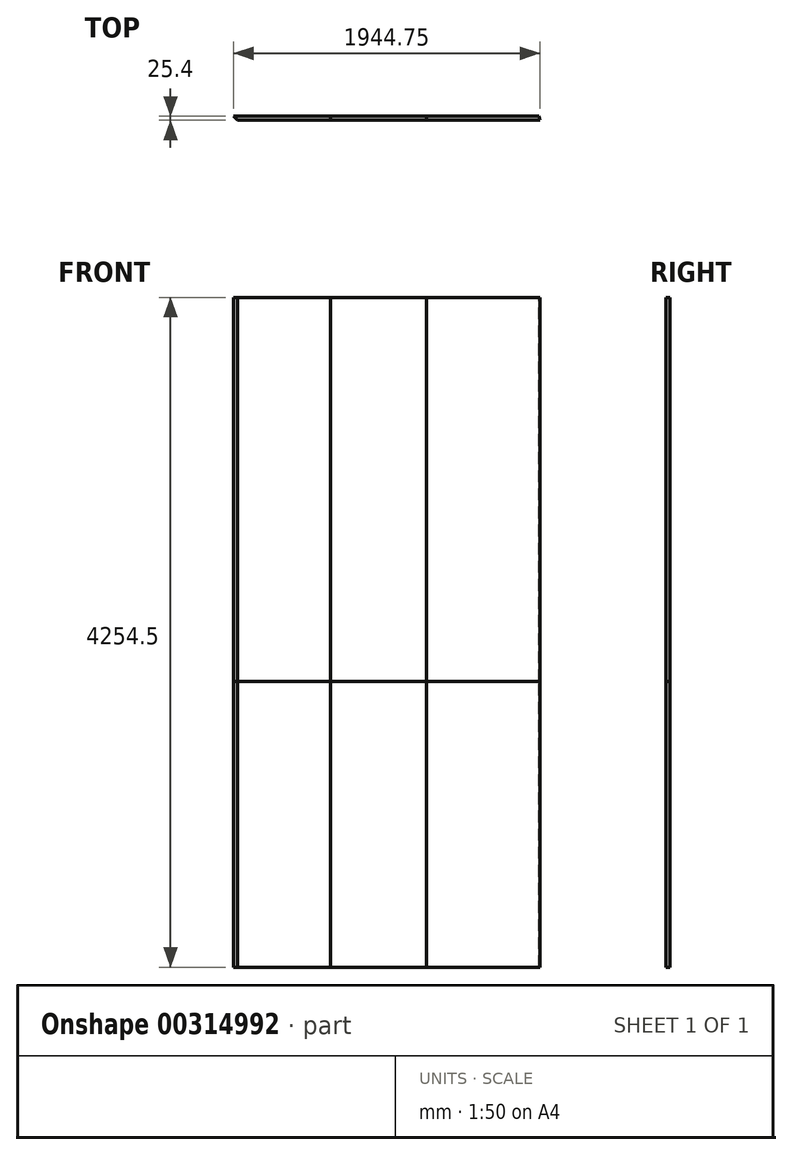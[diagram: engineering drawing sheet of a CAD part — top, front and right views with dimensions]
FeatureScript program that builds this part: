
annotation { "Feature Type Name" : "Feature", "Feature Type Description" : "" }
export const myFeature = defineFeature(function(context is Context, id is Id, definition is map)
    precondition{}
    {
        {
            var Q0;
            Q0=qCreatedBy(makeId("Top.planeOp"),FACE);
            var sketch = newSketch(context, id + "F0", { "sketchPlane" : qUnion([Q0])});
            skLineSegment(sketch, "E0", {"start": v(0, 0) * mm, "end": v(25.4, -25.4) * mm});
            skLineSegment(sketch, "E1", {"start": v(25.4, -25.4) * mm, "end": v(615.95, -25.4) * mm});
            skLineSegment(sketch, "E2", {"start": v(615.95, -25.4) * mm, "end": v(1225.55, -25.4) * mm});
            skLineSegment(sketch, "E3", {"start": v(1225.55, -25.4) * mm, "end": v(1944.75, -25.4) * mm});
            skLineSegment(sketch, "E4", {"start": v(1944.75, -25.4) * mm, "end": v(1944.75, 0) * mm, "construction": true});
            skLineSegment(sketch, "E5", {"start": v(1944.75, 0) * mm, "end": v(0, 0) * mm});
            skLineSegment(sketch, "E6", {"start": v(615.95, -25.4) * mm, "end": v(615.95, 0) * mm});
            skLineSegment(sketch, "E7", {"start": v(1502.86, -229.9) * mm, "end": v(1502.86, -380) * mm});
            skLineSegment(sketch, "E8", {"start": v(1225.55, 0) * mm, "end": v(1225.55, -25.4) * mm});
            skLineSegment(sketch, "E9", {"start": v(1944.75, -25.4) * mm, "end": v(1937.77, 0) * mm});
            skSolve(sketch);
        }
        {
            var Q0;
            {var subQ0=sQuery(id+"F0.wireOp",EDGE,"E0");Q0=makeQuery(id+"F0.imprint","IMPRINT",FACE,{"disambiguationData":[TD([[makeQuery(id+"F0.imprint","IMPRINT",EDGE,{"derivedFrom":subQ0}),1.0]])]});}
            extrude(context, id + "F1", {"entities" : qUnion([Q0]), "oppositeDirection" : true, "depth" : 2438.4 * mm});
        }
        {
            var Q0;
            Q0=makeQuery(id+"F0.imprint","IMPRINT",FACE,{"disambiguationData":[TD([[makeQuery(id+"F0.imprint","IMPRINT",EDGE,{"derivedFrom":sQuery(id+"F0.wireOp",EDGE,"E2")}),1.0]])]});
            var Q1;
            Q1=makeQuery(id+"F1.opExtrude","CAP_FACE",FACE,{"disambiguationData":[OSD([sQuery(id+"F0.wireOp",EDGE,"E0"),sQuery(id+"F0.wireOp",EDGE,"E1"),sQuery(id+"F0.wireOp",EDGE,"E5"),sQuery(id+"F0.wireOp",EDGE,"E6")])],"isStart":false});
            extrude(context, id + "F2", {"entities" : qUnion([Q0]), "endBound" : BoundingType.UP_TO_SURFACE, "oppositeDirection" : true, "endBoundEntityFace" : qUnion([Q1]), "depth" : 25.4 * mm});
        }
        {
            var Q0;
            Q0=makeQuery(id+"F0.imprint","IMPRINT",FACE,{"disambiguationData":[TD([[makeQuery(id+"F0.imprint","IMPRINT",EDGE,{"derivedFrom":sQuery(id+"F0.wireOp",EDGE,"E3")}),1.0]])]});
            var Q1;
            Q1=makeQuery(id+"F2.opExtrude","CAP_FACE",FACE,{"disambiguationData":[OSD([sQuery(id+"F0.wireOp",EDGE,"E0"),sQuery(id+"F0.wireOp",EDGE,"E1"),sQuery(id+"F0.wireOp",EDGE,"E5"),sQuery(id+"F0.wireOp",EDGE,"E6")])],"isStart":false});
            extrude(context, id + "F3", {"entities" : qUnion([Q0]), "endBound" : BoundingType.UP_TO_SURFACE, "oppositeDirection" : true, "endBoundEntityFace" : qUnion([Q1]), "depth" : 25.4 * mm});
        }
        {
            var Q0;
            Q0=makeQuery(id+"F1.opExtrude","CAP_FACE",FACE,{"disambiguationData":[OSD([sQuery(id+"F0.wireOp",EDGE,"E0"),sQuery(id+"F0.wireOp",EDGE,"E1"),sQuery(id+"F0.wireOp",EDGE,"E5"),sQuery(id+"F0.wireOp",EDGE,"E6")])],"isStart":false});
            extrude(context, id + "F4", {"entities" : qUnion([Q0]), "depth" : 1816.1 * mm});
        }
        {
            var Q0;
            Q0=makeQuery(id+"F2.opExtrude","CAP_FACE",FACE,{"disambiguationData":[OSD([sQuery(id+"F0.wireOp",EDGE,"E0"),sQuery(id+"F0.wireOp",EDGE,"E1"),sQuery(id+"F0.wireOp",EDGE,"E5"),sQuery(id+"F0.wireOp",EDGE,"E6")])],"isStart":false});
            var Q1;
            Q1=makeQuery(id+"F4.opExtrude","CAP_FACE",FACE,{"disambiguationData":[OSD([sQuery(id+"F0.wireOp",EDGE,"E0"),sQuery(id+"F0.wireOp",EDGE,"E1"),sQuery(id+"F0.wireOp",EDGE,"E5"),sQuery(id+"F0.wireOp",EDGE,"E6")])],"isStart":false});
            extrude(context, id + "F5", {"entities" : qUnion([Q0]), "endBound" : BoundingType.UP_TO_SURFACE, "endBoundEntityFace" : qUnion([Q1]), "depth" : 25.4 * mm});
        }
        {
            var Q0;
            Q0=makeQuery(id+"F3.opExtrude","CAP_FACE",FACE,{"disambiguationData":[OSD([sQuery(id+"F0.wireOp",EDGE,"E0"),sQuery(id+"F0.wireOp",EDGE,"E1"),sQuery(id+"F0.wireOp",EDGE,"E5"),sQuery(id+"F0.wireOp",EDGE,"E6")])],"isStart":false});
            var Q1;
            Q1=makeQuery(id+"F5.opExtrude","CAP_FACE",FACE,{"disambiguationData":[OSD([sQuery(id+"F0.wireOp",EDGE,"E0"),sQuery(id+"F0.wireOp",EDGE,"E1"),sQuery(id+"F0.wireOp",EDGE,"E5"),sQuery(id+"F0.wireOp",EDGE,"E6")])],"isStart":false});
            extrude(context, id + "F6", {"entities" : qUnion([Q0]), "endBound" : BoundingType.UP_TO_SURFACE, "endBoundEntityFace" : qUnion([Q1]), "depth" : 25.4 * mm});
        }
    });
